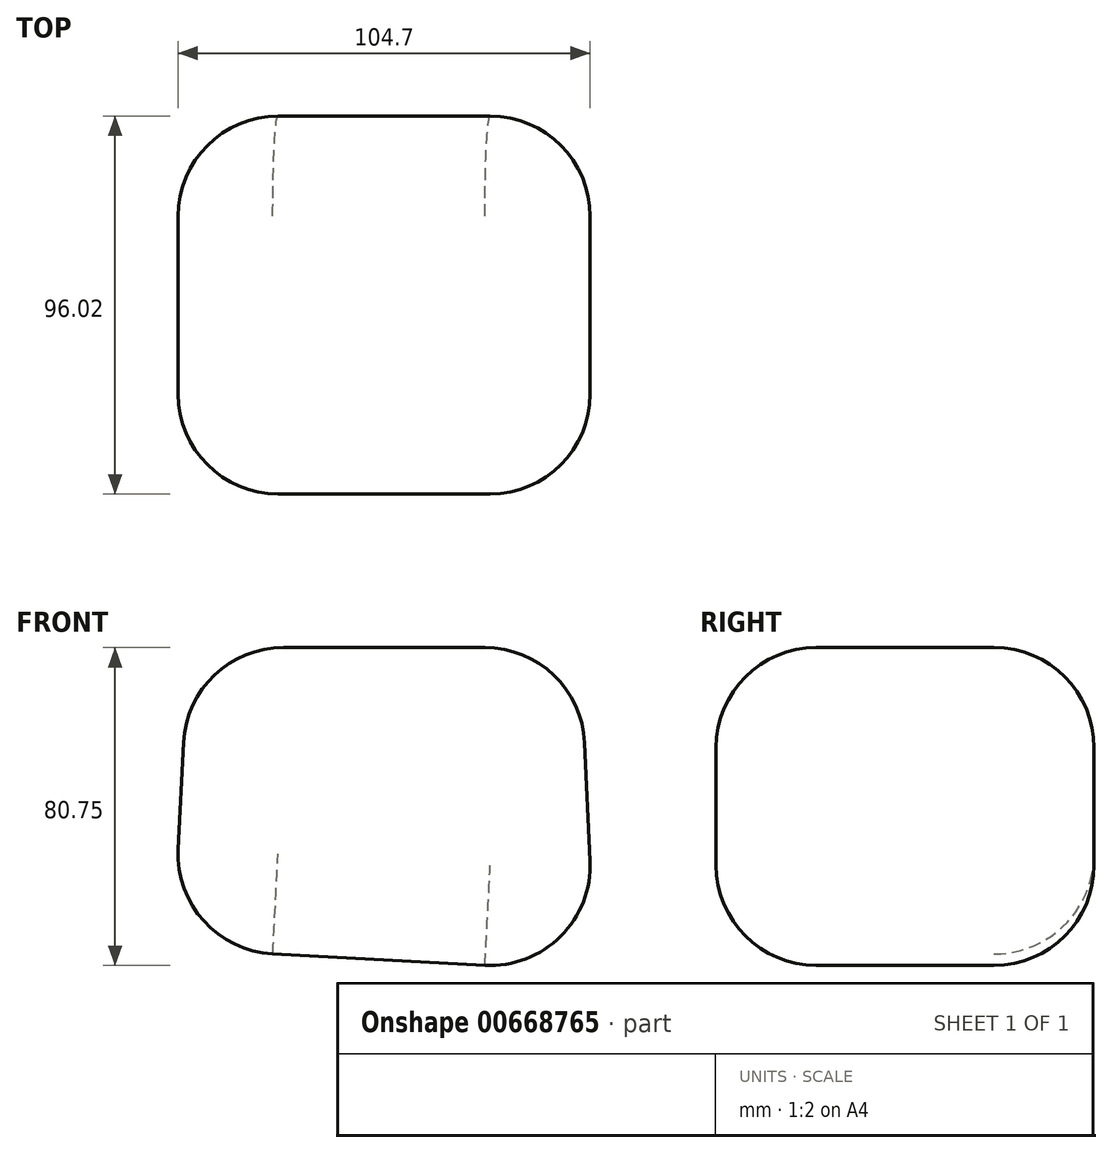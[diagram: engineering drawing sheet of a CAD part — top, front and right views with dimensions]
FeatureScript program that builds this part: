
annotation { "Feature Type Name" : "Feature", "Feature Type Description" : "" }
export const myFeature = defineFeature(function(context is Context, id is Id, definition is map)
    precondition{}
    {
        {
            var Q0;
            Q0=qCreatedBy(makeId("Front.planeOp"),FACE);
            var sketch = newSketch(context, id + "F0", { "sketchPlane" : qUnion([Q0])});
            skLineSegment(sketch, "E0", {"start": v(-62.44, 46) * mm, "end": v(37.15, 46) * mm});
            skLineSegment(sketch, "E1", {"start": v(37.15, 46) * mm, "end": v(40.94, -36.2) * mm});
            skLineSegment(sketch, "E2", {"start": v(40.94, -36.2) * mm, "end": v(-66.24, -30.51) * mm});
            skLineSegment(sketch, "E3", {"start": v(-66.24, -30.51) * mm, "end": v(-62.44, 46) * mm});
            skSolve(sketch);
        }
        {
            var Q0;
            Q0 = qSketchRegion(id + "F0", true);
            extrude(context, id + "F1", {"entities" : qUnion([Q0]), "endBound" : BoundingType.SYMMETRIC, "depth" : 96.01 * mm, "offsetDistance" : 25.4 * mm});
        }
        {
            var Q0;
            Q0=makeQuery(id+"F1.opExtrude","SWEPT_EDGE",EDGE,{"disambiguationData":[OSD([sQuery(id+"F0.wireOp",EDGE,"E0"),sQuery(id+"F0.wireOp",EDGE,"E1")])]});
            var Q1;
            Q1=makeQuery(id+"F1.opExtrude","SWEPT_EDGE",EDGE,{"disambiguationData":[OSD([sQuery(id+"F0.wireOp",EDGE,"E0"),sQuery(id+"F0.wireOp",EDGE,"E3")])]});
            var Q2;
            Q2=makeQuery(id+"F1.opExtrude","CAP_EDGE",EDGE,{"disambiguationData":[OSD([sQuery(id+"F0.wireOp",EDGE,"E0")])],"isStart":false});
            var Q3;
            Q3=makeQuery(id+"F1.opExtrude","CAP_EDGE",EDGE,{"disambiguationData":[OSD([sQuery(id+"F0.wireOp",EDGE,"E0")])],"isStart":true});
            var Q4;
            Q4=makeQuery(id+"F1.opExtrude","CAP_FACE",FACE,{"disambiguationData":[OSD([sQuery(id+"F0.wireOp",EDGE,"E0"),sQuery(id+"F0.wireOp",EDGE,"E1"),sQuery(id+"F0.wireOp",EDGE,"E2"),sQuery(id+"F0.wireOp",EDGE,"E3")])],"isStart":true});
            fillet(context, id + "F2", {"entities" : qUnion([Q0, Q1, Q2, Q3, Q4]), "radius" : 25.4 * mm, "tangentPropagation" : true, "allowEdgeOverflow" : false});
        }
        {
            var Q0;
            Q0=makeQuery(id+"F1.opExtrude","CAP_EDGE",EDGE,{"disambiguationData":[OSD([sQuery(id+"F0.wireOp",EDGE,"E1")])],"isStart":false});
            var Q1;
            {var subQ0=sQuery(id+"F0.wireOp",EDGE,"E0");Q1=makeQuery(id+"F2.opFillet","BLEND_EDGE",EDGE,{"blendedFrom":[makeQuery(id+"F1.opExtrude","SWEPT_EDGE",EDGE,{"disambiguationData":[OSD([subQ0,sQuery(id+"F0.wireOp",EDGE,"E1")])]}),makeQuery(id+"F1.opExtrude","CAP_EDGE",EDGE,{"disambiguationData":[OSD([subQ0])],"isStart":false})],"blendedInto":[]});}
            var Q2;
            {var subQ0=sQuery(id+"F0.wireOp",EDGE,"E0");Q2=makeQuery(id+"F2.opFillet","BLEND_EDGE",EDGE,{"blendedFrom":[makeQuery(id+"F1.opExtrude","SWEPT_EDGE",EDGE,{"disambiguationData":[OSD([subQ0,sQuery(id+"F0.wireOp",EDGE,"E3")])]}),makeQuery(id+"F1.opExtrude","CAP_EDGE",EDGE,{"disambiguationData":[OSD([subQ0])],"isStart":false})],"blendedInto":[]});}
            fillet(context, id + "F3", {"entities" : qUnion([Q0, Q1, Q2]), "radius" : 25.4 * mm, "tangentPropagation" : true, "allowEdgeOverflow" : false});
        }
        {
            var Q0;
            Q0=makeQuery(id+"F2.opFillet","BLEND_FACE",FACE,{"disambiguationData":[OSD([sQuery(id+"F0.wireOp",EDGE,"E2")])]});
            var Q1;
            Q1=makeQuery(id+"F1.opExtrude","CAP_EDGE",EDGE,{"disambiguationData":[OSD([sQuery(id+"F0.wireOp",EDGE,"E2")])],"isStart":false});
            fillet(context, id + "F4", {"entities" : qUnion([Q0, Q1]), "radius" : 25.4 * mm, "tangentPropagation" : true, "allowEdgeOverflow" : false});
        }
    });
